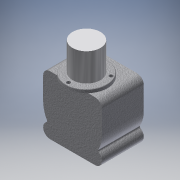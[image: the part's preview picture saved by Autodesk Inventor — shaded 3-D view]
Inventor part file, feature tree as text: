
AUTODESK INVENTOR PART (.ipt)
format: ipt  version: 2016 (Build 200138000, 138)  size: 190,976 bytes
history: native  units: in
note: dims shown in document units (in); Inventor stores cm internally (conversion verified against a paired STEP export)
features: sketch x5, extrude x4, fillet x3, reference x3, projected_geometry x2, hole x1
ambient origin geometry x8: Origin, YZ Plane, XZ Plane, XY Plane, X Axis, Y Axis, Z Axis, Center Point
bodies: Solid1 (feature_tree)
feature tree (18):
  extrude  "Extrusion1"  Depth=2.11in
  fillet  "Fillet1"  Radius=1.5in
  extrude  "Extrusion2"  Depth=0.5in
  fillet  "Fillet2"  Radius=0.5in
  extrude  "Extrusion3"  Depth=1.055in
  fillet  "Fillet3"  Radius=1.0in
  extrude  "Extrusion4"  Depth=1.5in
  hole  "Hole1"  [1 undecoded]
  sketch  "Sketch1"  dims[d0=2.11in d1=2.11in d2=1.5in d3=0.0in]
  sketch  "Sketch3"  dims[d4=0.25in d8=2.0in d9=0.5in]
  sketch  "Sketch4"  dims[d10=0.5in d12=1.055in d13=1.0in d14=0.0in]
  projected_geometry  "Projected Loop1"
  projected_geometry  "Projected Loop2"
  sketch  "Sketch5"  dims[d15=0.0625in d16=1.5in]
  sketch  "Sketch6"  dims[d17=0.25in d18=0.125in d19=0.0in d20=0.0312in d22=1.0in d23=0.0in d24=0.25in d25=0.129in d26=0.75in d27=0.225in d28=0.25in d29=0.5635in d30=0.25in d31=0.8108in]
  reference  "Reference1"
  reference  "Reference2"
  reference  "Reference3"
note: 1 required parameter value undecoded (feature->parameter linkage not recoverable at this tier; creation-order binding heuristic only, values carry confidence <= 0.55)
